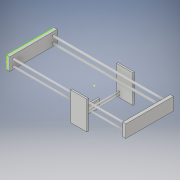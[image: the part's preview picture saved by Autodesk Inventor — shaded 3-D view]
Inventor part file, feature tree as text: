
AUTODESK INVENTOR PART (.ipt)
format: ipt  version: 2019 (Build 230136000, 136)  size: 150,016 bytes
history: native  units: mm
features: sketch x10, extrude x8
ambient origin geometry x8: Origin, YZ Plane, XZ Plane, XY Plane, X Axis, Y Axis, Z Axis, Center Point
bodies: Solid1 (feature_tree)
feature tree (18):
  extrude  "Extrusion1"  Depth=71.0mm TaperAngle=0.0deg
  extrude  "Extrusion2"  Depth=1.0mm TaperAngle=0.0deg
  extrude  "Extrusion3"  Depth=1.0mm TaperAngle=0.0deg
  sketch  "Sketch4"  dims[d12=28.0mm d13=0.0mm d14=1.0mm d15=0.0mm]
  extrude  "Extrusion4"  Depth=1.0mm TaperAngle=0.0deg
  extrude  "Extrusion5"  [1 undecoded]
  extrude  "Extrusion6"  [1 undecoded]
  extrude  "Extrusion7"  [1 undecoded]
  sketch  "Sketch9"
  extrude  "Extrusion8"  [1 undecoded]
  sketch  "Sketch1"  dims[d0=2.0mm d1=0.0mm d2=71.0mm d3=0.0mm]
  sketch  "Sketch2"  dims[d4=2.0mm d5=0.0mm d6=1.0mm d7=0.0mm]
  sketch  "Sketch3"  dims[d8=1.0mm d9=0.0mm d10=28.0mm d11=0.0mm]
  sketch  "Sketch5"
  sketch  "Sketch6"
  sketch  "Sketch7"
  sketch  "Sketch8"
  sketch  "Sketch10"
note: 4 required parameter values undecoded (feature->parameter linkage not recoverable at this tier; creation-order binding heuristic only, values carry confidence <= 0.55)
